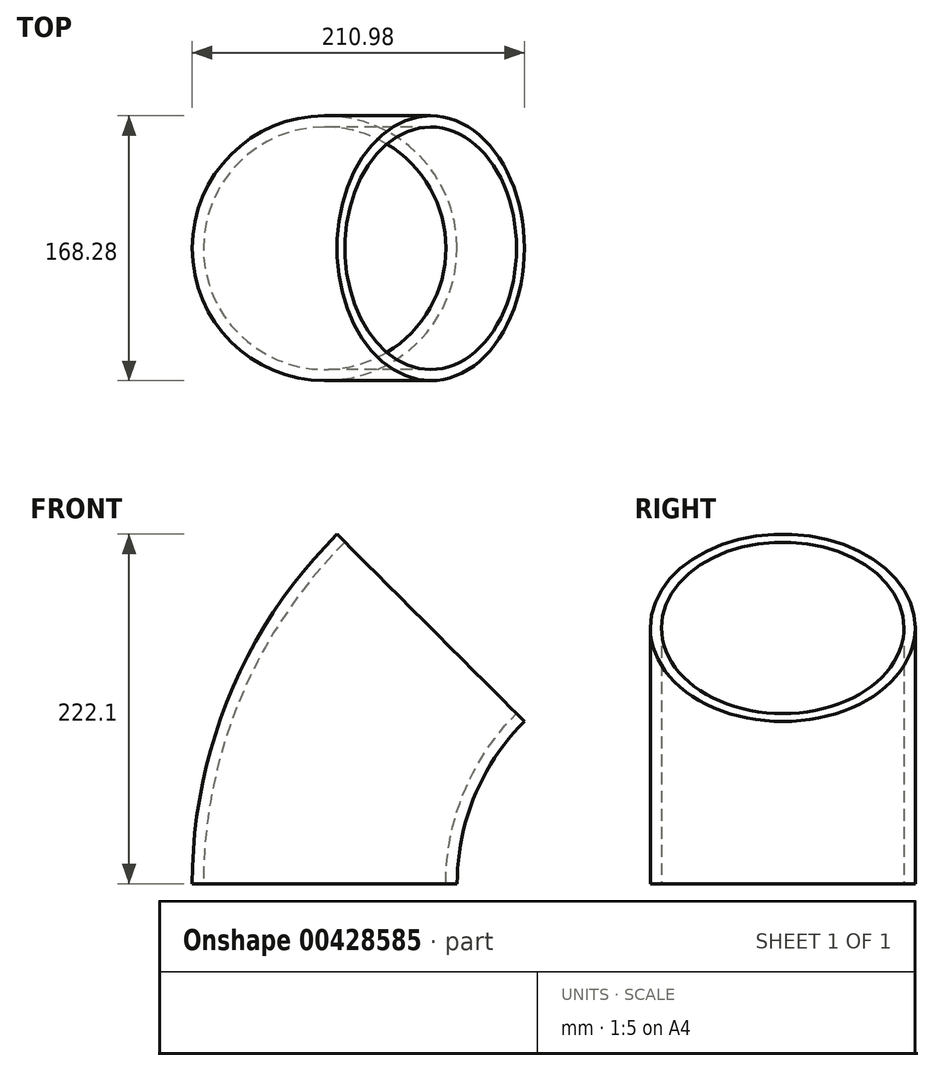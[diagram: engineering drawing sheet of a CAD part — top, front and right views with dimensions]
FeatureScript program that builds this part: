
annotation { "Feature Type Name" : "Feature", "Feature Type Description" : "" }
export const myFeature = defineFeature(function(context is Context, id is Id, definition is map)
    precondition{}
    {
        {
            var Q0;
            Q0=qCreatedBy(makeId("Front.planeOp"),FACE);
            var sketch = newSketch(context, id + "F0", { "sketchPlane" : qUnion([Q0])});
            skArc(sketch, "E0", {"start": v(-229.95, 0) * mm, "mid": v(-212.45, 88) * mm, "end": v(-162.6, 162.6) * mm});
            skLineSegment(sketch, "E1", {"start": v(-229.95, 0) * mm, "end": v(0, 0) * mm});
            skLineSegment(sketch, "E2", {"start": v(-162.6, 162.6) * mm, "end": v(0, 0) * mm});
            skLineSegment(sketch, "E3", {"start": v(-229.95, 0) * mm, "end": v(-229.95, 95.25) * mm});
            skLineSegment(sketch, "E4", {"start": v(-229.95, 95.25) * mm, "end": v(-162.6, 162.6) * mm});
            skSolve(sketch);
        }
        {
            var Q0;
            Q0=qCreatedBy(makeId("Top.planeOp"),FACE);
            var sketch = newSketch(context, id + "F1", { "sketchPlane" : qUnion([Q0])});
            skCircle(sketch, "E5", {"center": v(-229.95, 0) * mm, "radius": 84.14 * mm});
            skCircle(sketch, "E6.0", {"center": v(-229.95, 0) * mm, "radius": 77.03 * mm});
            skSolve(sketch);
        }
        {
            var Q0;
            Q0=makeQuery(id+"F1.imprint","IMPRINT",FACE,{"disambiguationData":[TD([[makeQuery(id+"F1.imprint","IMPRINT",EDGE,{"derivedFrom":sQuery(id+"F1.wireOp",EDGE,"E5")}),1.0]])]});
            var Q1;
            Q1=sQuery(id+"F0.wireOp",EDGE,"E0");
            sweep(context, id + "F2", {"profiles" : qUnion([Q0]), "path" : qUnion([Q1])});
        }
    });
